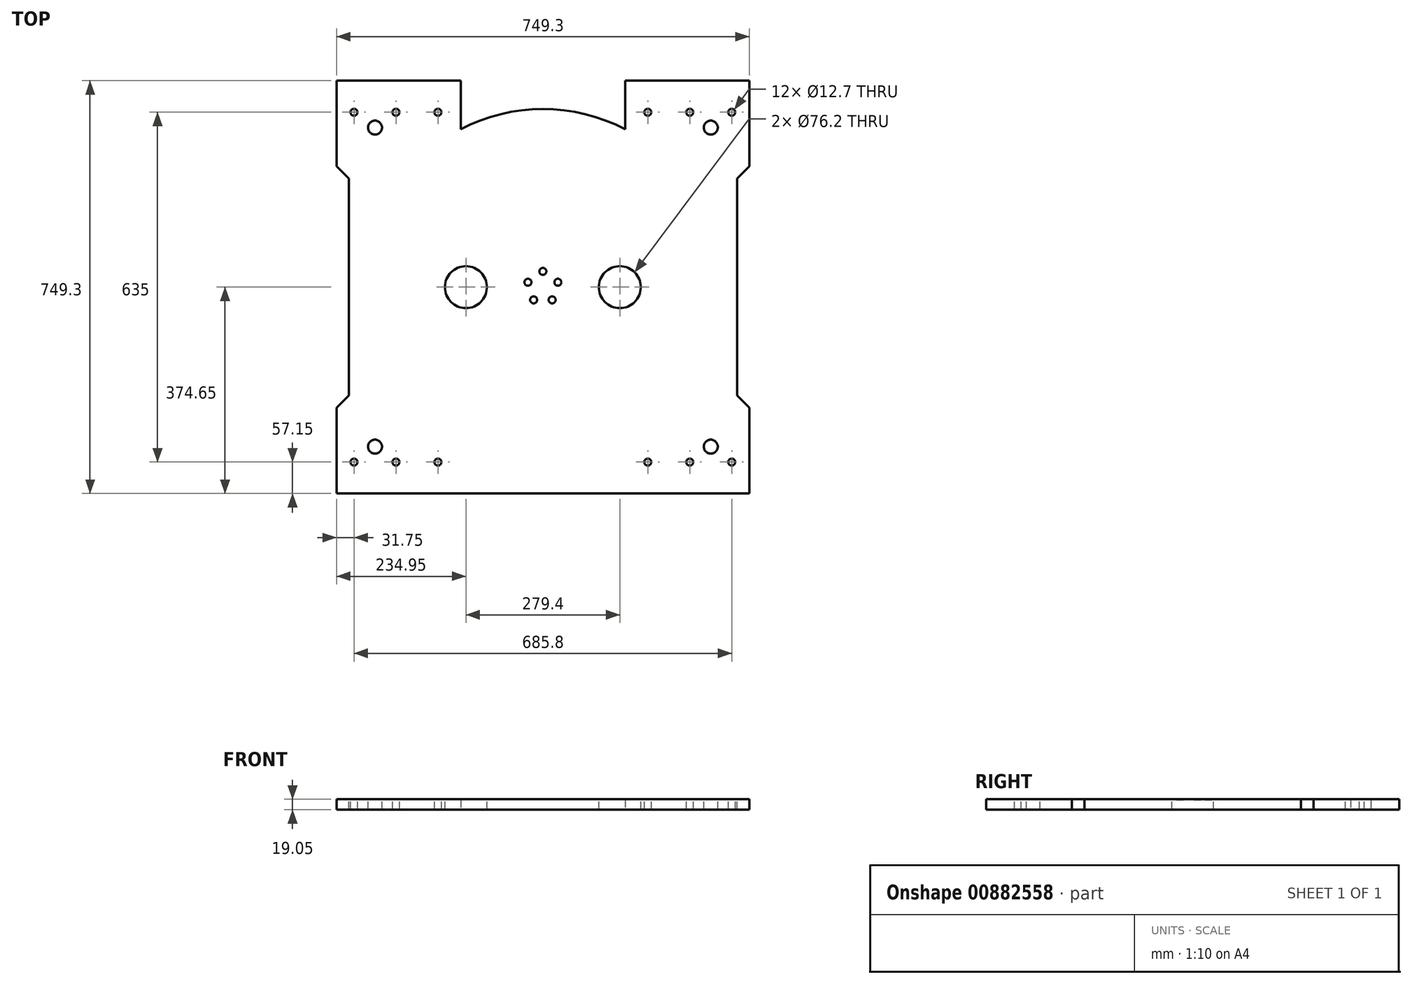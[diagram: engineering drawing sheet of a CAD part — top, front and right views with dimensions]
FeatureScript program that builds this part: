
annotation { "Feature Type Name" : "Feature", "Feature Type Description" : "" }
export const myFeature = defineFeature(function(context is Context, id is Id, definition is map)
    precondition{}
    {
        {
            var Q0;
            Q0=qCreatedBy(makeId("Top.planeOp"),FACE);
            var sketch = newSketch(context, id + "F0", { "sketchPlane" : qUnion([Q0])});
            skLineSegment(sketch, "E0.bottom", {"start": v(374.65, -374.65) * mm, "end": v(-374.65, -374.65) * mm});
            skLineSegment(sketch, "E0.top", {"start": v(374.65, 374.65) * mm, "end": v(-374.65, 374.65) * mm});
            skLineSegment(sketch, "E0.left", {"start": v(374.65, -374.65) * mm, "end": v(374.65, 374.65) * mm});
            skLineSegment(sketch, "E0.right", {"start": v(-374.65, -374.65) * mm, "end": v(-374.65, 374.65) * mm});
            skPoint(sketch, "E0.middle", {"position": v(0, 0) * mm});
            skSolve(sketch);
        }
        {
            var Q0;
            Q0 = qSketchRegion(id + "F0", true);
            extrude(context, id + "F1", {"entities" : qUnion([Q0]), "depth" : 19.05 * mm, "offsetDistance" : 25.4 * mm});
        }
        {
            var Q0;
            Q0=makeQuery(id+"F1.opExtrude","CAP_FACE",FACE,{"disambiguationData":[OSD([sQuery(id+"F0.wireOp",EDGE,"E0.bottom"),sQuery(id+"F0.wireOp",EDGE,"E0.top"),sQuery(id+"F0.wireOp",EDGE,"E0.left"),sQuery(id+"F0.wireOp",EDGE,"E0.right")])],"isStart":false});
            var sketch = newSketch(context, id + "F2", { "sketchPlane" : qUnion([Q0])});
            skLineSegment(sketch, "E1", {"start": v(0, 0) * mm, "end": v(-374.65, 0) * mm, "construction": true});
            skPoint(sketch, "E2", {"position": v(-374.65, 219.08) * mm});
            skPoint(sketch, "E3", {"position": v(-374.65, 196.85) * mm});
            skPoint(sketch, "E4.MirrorP", {"position": v(-374.65, -219.07) * mm});
            skPoint(sketch, "E5.MirrorP", {"position": v(-374.65, -196.85) * mm});
            skLineSegment(sketch, "E6", {"start": v(-374.65, 219.08) * mm, "end": v(-352.43, 196.85) * mm});
            skLineSegment(sketch, "E7.MirrorCS", {"start": v(-374.65, -219.07) * mm, "end": v(-352.43, -196.85) * mm});
            skLineSegment(sketch, "E8", {"start": v(-352.43, 196.85) * mm, "end": v(-352.43, -196.85) * mm});
            skLineSegment(sketch, "E9", {"start": v(-374.65, 219.08) * mm, "end": v(-374.65, -219.07) * mm});
            skLineSegment(sketch, "E10", {"start": v(0, 0) * mm, "end": v(0, 374.65) * mm, "construction": true});
            skLineSegment(sketch, "E11.MirrorCS", {"start": v(352.42, 196.85) * mm, "end": v(352.43, -196.85) * mm});
            skPoint(sketch, "E12.MirrorP", {"position": v(374.65, 219.08) * mm});
            skLineSegment(sketch, "E13.MirrorCS", {"start": v(374.65, 219.08) * mm, "end": v(352.42, 196.85) * mm});
            skLineSegment(sketch, "E14.MirrorCS", {"start": v(374.65, 219.08) * mm, "end": v(374.65, -219.07) * mm});
            skLineSegment(sketch, "E15.MirrorCS", {"start": v(374.65, -219.07) * mm, "end": v(352.43, -196.85) * mm});
            skSolve(sketch);
        }
        {
            var Q0;
            Q0=makeQuery(id+"F2.imprint","IMPRINT",FACE,{"disambiguationData":[TD([[makeQuery(id+"F2.imprint","IMPRINT",EDGE,{"derivedFrom":sQuery(id+"F2.wireOp",EDGE,"E6")}),-1.0]])]});
            var Q1;
            Q1=makeQuery(id+"F2.imprint","IMPRINT",FACE,{"disambiguationData":[TD([[makeQuery(id+"F2.imprint","IMPRINT",EDGE,{"derivedFrom":sQuery(id+"F2.wireOp",EDGE,"E11.MirrorCS")}),1.0]])]});
            var Q2;
            Q2=sQuery(id+"F2.wireOp",EDGE,"E8");
            var Q3;
            Q3=sQuery(id+"F2.wireOp",EDGE,"E6");
            var Q4;
            Q4=sQuery(id+"F2.wireOp",EDGE,"E9");
            var Q5;
            Q5=sQuery(id+"F2.wireOp",EDGE,"E7.MirrorCS");
            var Q6;
            Q6=sQuery(id+"F2.wireOp",EDGE,"E13.MirrorCS");
            var Q7;
            Q7=sQuery(id+"F2.wireOp",EDGE,"E11.MirrorCS");
            var Q8;
            Q8=sQuery(id+"F2.wireOp",EDGE,"E14.MirrorCS");
            var Q9;
            Q9=sQuery(id+"F2.wireOp",EDGE,"E15.MirrorCS");
            extrude(context, id + "F3", {"entities" : qUnion([Q0, Q1]), "operationType" : NewBodyOperationType.REMOVE, "surfaceEntities" : qUnion([Q2, Q3, Q4, Q5, Q6, Q7, Q8, Q9]), "oppositeDirection" : true, "depth" : 114.3 * mm, "offsetDistance" : 25.4 * mm});
        }
        {
            var Q0;
            Q0=makeQuery(id+"F1.opExtrude","CAP_FACE",FACE,{"disambiguationData":[OSD([sQuery(id+"F0.wireOp",EDGE,"E0.bottom"),sQuery(id+"F0.wireOp",EDGE,"E0.top"),sQuery(id+"F0.wireOp",EDGE,"E0.left"),sQuery(id+"F0.wireOp",EDGE,"E0.right")])],"isStart":false});
            var sketch = newSketch(context, id + "F4", { "sketchPlane" : qUnion([Q0])});
            skLineSegment(sketch, "E16", {"start": v(0, 374.65) * mm, "end": v(0, -374.65) * mm, "construction": true});
            skLineSegment(sketch, "E17", {"start": v(352.43, 0) * mm, "end": v(-352.43, 0) * mm, "construction": true});
            skCircle(sketch, "E18", {"center": v(0, 0) * mm, "radius": 28.58 * mm, "construction": true});
            skCircle(sketch, "E19", {"center": v(0, 28.58) * mm, "radius": 6.35 * mm});
            skCircle(sketch, "E20.1.0", {"center": v(-27.18, 8.83) * mm, "radius": 6.35 * mm});
            skCircle(sketch, "E20.2.0", {"center": v(-16.8, -23.12) * mm, "radius": 6.35 * mm});
            skCircle(sketch, "E20.3.0", {"center": v(16.8, -23.12) * mm, "radius": 6.35 * mm});
            skCircle(sketch, "E20.4.0", {"center": v(27.18, 8.83) * mm, "radius": 6.35 * mm});
            skSolve(sketch);
        }
        {
            var Q0;
            Q0 = qSketchRegion(id + "F4", true);
            extrude(context, id + "F5", {"entities" : qUnion([Q0]), "operationType" : NewBodyOperationType.REMOVE, "oppositeDirection" : true, "depth" : 1.27 * mm, "offsetDistance" : 25.4 * mm});
        }
        {
            var Q0;
            Q0=makeQuery(id+"F1.opExtrude","CAP_FACE",FACE,{"disambiguationData":[OSD([sQuery(id+"F0.wireOp",EDGE,"E0.bottom"),sQuery(id+"F0.wireOp",EDGE,"E0.top"),sQuery(id+"F0.wireOp",EDGE,"E0.left"),sQuery(id+"F0.wireOp",EDGE,"E0.right")])],"isStart":false});
            var sketch = newSketch(context, id + "F6", { "sketchPlane" : qUnion([Q0])});
            skLineSegment(sketch, "E21", {"start": v(0, 374.65) * mm, "end": v(0, -374.65) * mm, "construction": true});
            skLineSegment(sketch, "E22", {"start": v(352.43, 0) * mm, "end": v(-352.43, 0) * mm, "construction": true});
            skLineSegment(sketch, "E23", {"start": v(0, -317.5) * mm, "end": v(374.65, -317.5) * mm, "construction": true});
            skCircle(sketch, "E24", {"center": v(190.5, -317.5) * mm, "radius": 6.35 * mm});
            skCircle(sketch, "E25.1.0.0", {"center": v(266.7, -317.5) * mm, "radius": 6.35 * mm});
            skCircle(sketch, "E25.2.0.0", {"center": v(342.9, -317.5) * mm, "radius": 6.35 * mm});
            skLineSegment(sketch, "E25.direction1", {"start": v(190.5, -317.5) * mm, "end": v(266.7, -317.5) * mm, "construction": true});
            skCircle(sketch, "E26", {"center": v(304.8, -289.56) * mm, "radius": 12.7 * mm});
            skCircle(sketch, "E27.MirrorC", {"center": v(304.8, 289.56) * mm, "radius": 12.7 * mm});
            skCircle(sketch, "E28.MirrorC", {"center": v(342.9, 317.5) * mm, "radius": 6.35 * mm});
            skCircle(sketch, "E29.MirrorC", {"center": v(266.7, 317.5) * mm, "radius": 6.35 * mm});
            skCircle(sketch, "E30.MirrorC", {"center": v(190.5, 317.5) * mm, "radius": 6.35 * mm});
            skCircle(sketch, "E31.MirrorC", {"center": v(-304.8, -289.56) * mm, "radius": 12.7 * mm});
            skCircle(sketch, "E32.MirrorC", {"center": v(-342.9, -317.5) * mm, "radius": 6.35 * mm});
            skCircle(sketch, "E33.MirrorC", {"center": v(-266.7, -317.5) * mm, "radius": 6.35 * mm});
            skCircle(sketch, "E34.MirrorC", {"center": v(-190.5, -317.5) * mm, "radius": 6.35 * mm});
            skCircle(sketch, "E35.MirrorC", {"center": v(-190.5, 317.5) * mm, "radius": 6.35 * mm});
            skCircle(sketch, "E36.MirrorC", {"center": v(-266.7, 317.5) * mm, "radius": 6.35 * mm});
            skCircle(sketch, "E37.MirrorC", {"center": v(-342.9, 317.5) * mm, "radius": 6.35 * mm});
            skCircle(sketch, "E38.MirrorC", {"center": v(-304.8, 289.56) * mm, "radius": 12.7 * mm});
            skCircle(sketch, "E39", {"center": v(-139.7, 0) * mm, "radius": 38.1 * mm});
            skCircle(sketch, "E40.MirrorC", {"center": v(139.7, 0) * mm, "radius": 38.1 * mm});
            skSolve(sketch);
        }
        {
            var Q0;
            Q0 = qSketchRegion(id + "F6", true);
            extrude(context, id + "F7", {"entities" : qUnion([Q0]), "operationType" : NewBodyOperationType.REMOVE, "oppositeDirection" : true, "depth" : 25.4 * mm, "offsetDistance" : 25.4 * mm});
        }
        {
            var Q0;
            Q0=makeQuery(id+"F1.opExtrude","CAP_FACE",FACE,{"disambiguationData":[OSD([sQuery(id+"F0.wireOp",EDGE,"E0.bottom"),sQuery(id+"F0.wireOp",EDGE,"E0.top"),sQuery(id+"F0.wireOp",EDGE,"E0.left"),sQuery(id+"F0.wireOp",EDGE,"E0.right")])],"isStart":true});
            var sketch = newSketch(context, id + "F8", { "sketchPlane" : qUnion([Q0])});
            skLineSegment(sketch, "E41", {"start": v(0, 0) * mm, "end": v(0, -374.65) * mm, "construction": true});
            skLineSegment(sketch, "E42", {"start": v(0, -374.65) * mm, "end": v(-149.23, -374.65) * mm});
            skLineSegment(sketch, "E43.MirrorCS", {"start": v(0, -374.65) * mm, "end": v(149.22, -374.65) * mm});
            skLineSegment(sketch, "E44", {"start": v(-149.23, -374.65) * mm, "end": v(-149.23, -287.42) * mm});
            skLineSegment(sketch, "E45", {"start": v(149.23, -374.65) * mm, "end": v(149.22, -287.42) * mm});
            skArc(sketch, "E46", {"start": v(-149.23, -286.7) * mm, "mid": v(0, -323.22) * mm, "end": v(149.22, -286.7) * mm});
            skLineSegment(sketch, "E47", {"start": v(-149.23, -287.42) * mm, "end": v(-149.23, -286.7) * mm});
            skLineSegment(sketch, "E48", {"start": v(149.22, -286.7) * mm, "end": v(149.22, -287.42) * mm});
            skSolve(sketch);
        }
        {
            var Q0;
            Q0 = qSketchRegion(id + "F8", true);
            extrude(context, id + "F9", {"entities" : qUnion([Q0]), "operationType" : NewBodyOperationType.REMOVE, "oppositeDirection" : true, "depth" : 37.6 * mm, "offsetDistance" : 25.4 * mm});
        }
    });
